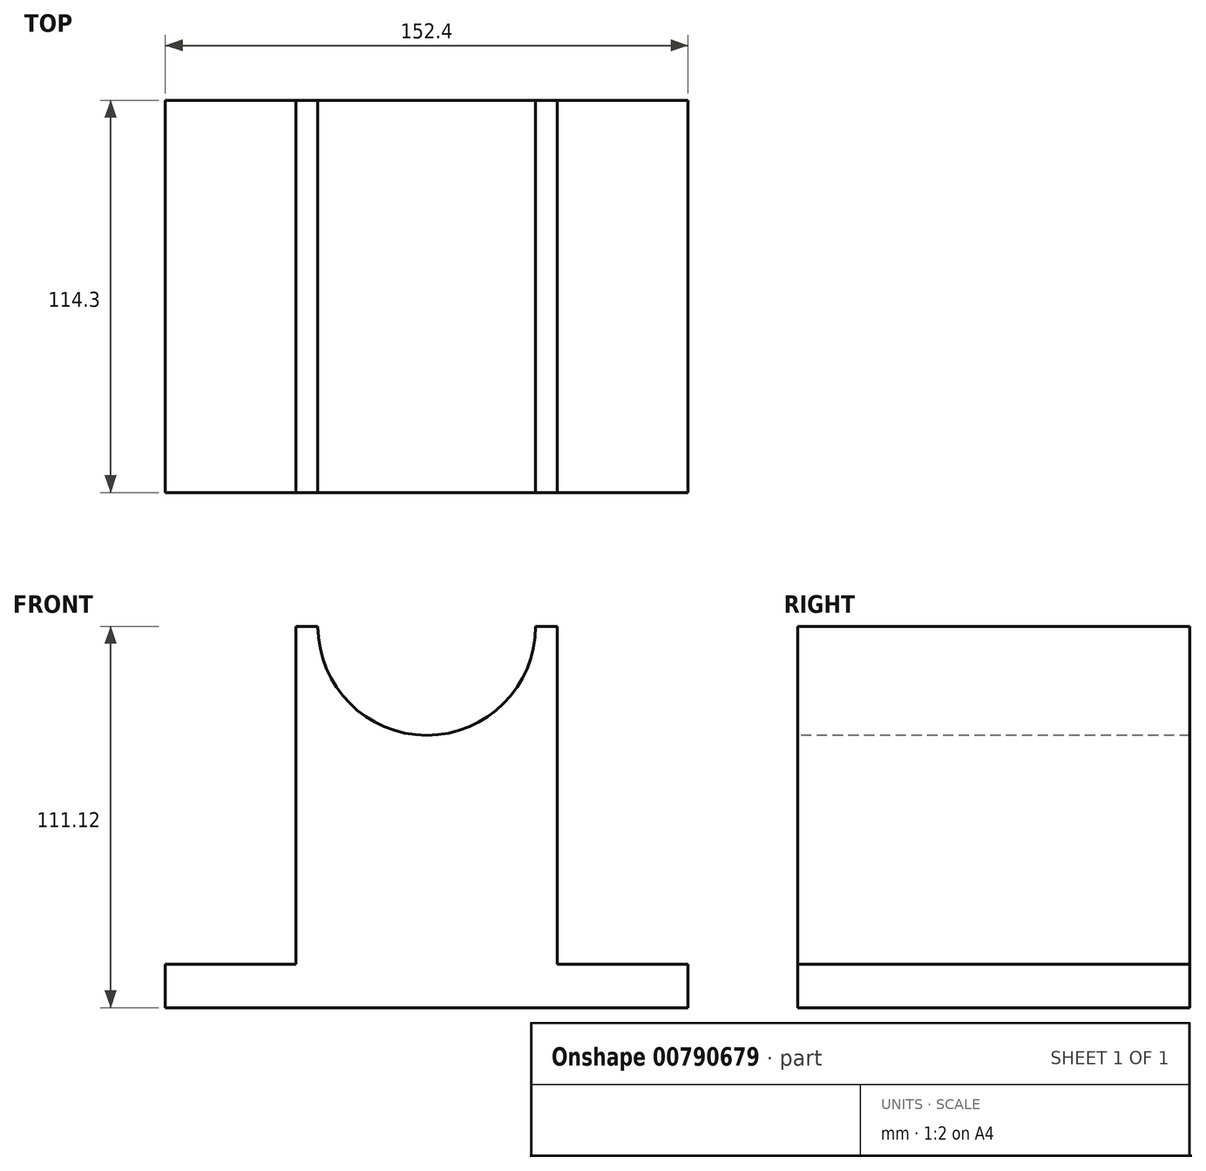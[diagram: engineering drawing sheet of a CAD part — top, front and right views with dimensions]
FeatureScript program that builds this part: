
annotation { "Feature Type Name" : "Feature", "Feature Type Description" : "" }
export const myFeature = defineFeature(function(context is Context, id is Id, definition is map)
    precondition{}
    {
        {
            var Q0;
            Q0=qCreatedBy(makeId("Front.planeOp"),FACE);
            var sketch = newSketch(context, id + "F0", { "sketchPlane" : qUnion([Q0])});
            skLineSegment(sketch, "E0", {"start": v(0, 0) * mm, "end": v(76.2, 0) * mm});
            skLineSegment(sketch, "E1", {"start": v(0, 0) * mm, "end": v(-76.2, 0) * mm});
            skLineSegment(sketch, "E2", {"start": v(-76.2, 0) * mm, "end": v(-76.2, 12.7) * mm});
            skLineSegment(sketch, "E3", {"start": v(-76.2, 12.7) * mm, "end": v(-38.1, 12.7) * mm});
            skLineSegment(sketch, "E4", {"start": v(-38.1, 12.7) * mm, "end": v(-38.1, 111.13) * mm});
            skPoint(sketch, "E5.startSnap0", {"position": v(38.1, 0) * mm});
            skLineSegment(sketch, "E6", {"start": v(-38.1, 111.13) * mm, "end": v(38.1, 111.13) * mm});
            skLineSegment(sketch, "E7", {"start": v(38.1, 111.13) * mm, "end": v(38.1, 12.7) * mm});
            skLineSegment(sketch, "E8", {"start": v(38.1, 12.7) * mm, "end": v(76.2, 12.7) * mm});
            skLineSegment(sketch, "E9", {"start": v(76.2, 12.7) * mm, "end": v(76.2, 0) * mm});
            skSolve(sketch);
        }
        {
            var Q0;
            Q0=makeQuery(id+"F0.imprint","IMPRINT",FACE,{"disambiguationData":[TD([[makeQuery(id+"F0.imprint","IMPRINT",EDGE,{"derivedFrom":sQuery(id+"F0.wireOp",EDGE,"E0")}),1.0]])]});
            extrude(context, id + "F1", {"entities" : qUnion([Q0]), "depth" : 114.3 * mm, "offsetDistance" : 25.4 * mm});
        }
        {
            var Q0;
            Q0=makeQuery(id+"F1.opExtrude","CAP_FACE",FACE,{"disambiguationData":[OSD([sQuery(id+"F0.wireOp",EDGE,"E0"),sQuery(id+"F0.wireOp",EDGE,"E1"),sQuery(id+"F0.wireOp",EDGE,"E2"),sQuery(id+"F0.wireOp",EDGE,"E3"),sQuery(id+"F0.wireOp",EDGE,"E4"),sQuery(id+"F0.wireOp",EDGE,"E6"),sQuery(id+"F0.wireOp",EDGE,"E7"),sQuery(id+"F0.wireOp",EDGE,"E8"),sQuery(id+"F0.wireOp",EDGE,"E9")])],"isStart":false});
            var sketch = newSketch(context, id + "F2", { "sketchPlane" : qUnion([Q0])});
            skLineSegment(sketch, "E10", {"start": v(-38.1, 111.13) * mm, "end": v(-31.75, 111.13) * mm});
            skLineSegment(sketch, "E11", {"start": v(38.1, 111.13) * mm, "end": v(31.75, 111.13) * mm});
            skLineSegment(sketch, "E12", {"start": v(-31.75, 111.13) * mm, "end": v(0, 111.13) * mm});
            skArc(sketch, "E13", {"start": v(-31.75, 111.12) * mm, "mid": v(0, 79.37) * mm, "end": v(31.75, 111.12) * mm});
            skSolve(sketch);
        }
        {
            var Q0;
            {var subQ0=sQuery(id+"F2.wireOp",EDGE,"E12");Q0=makeQuery(id+"F2.imprint","IMPRINT",FACE,{"disambiguationData":[TD([[makeQuery(id+"F2.imprint","IMPRINT",EDGE,{"derivedFrom":subQ0}),-1.0]])]});}
            extrude(context, id + "F3", {"entities" : qUnion([Q0]), "operationType" : NewBodyOperationType.REMOVE, "endBound" : BoundingType.THROUGH_ALL, "oppositeDirection" : true, "depth" : 25.4 * mm, "offsetDistance" : 25.4 * mm});
        }
    });
